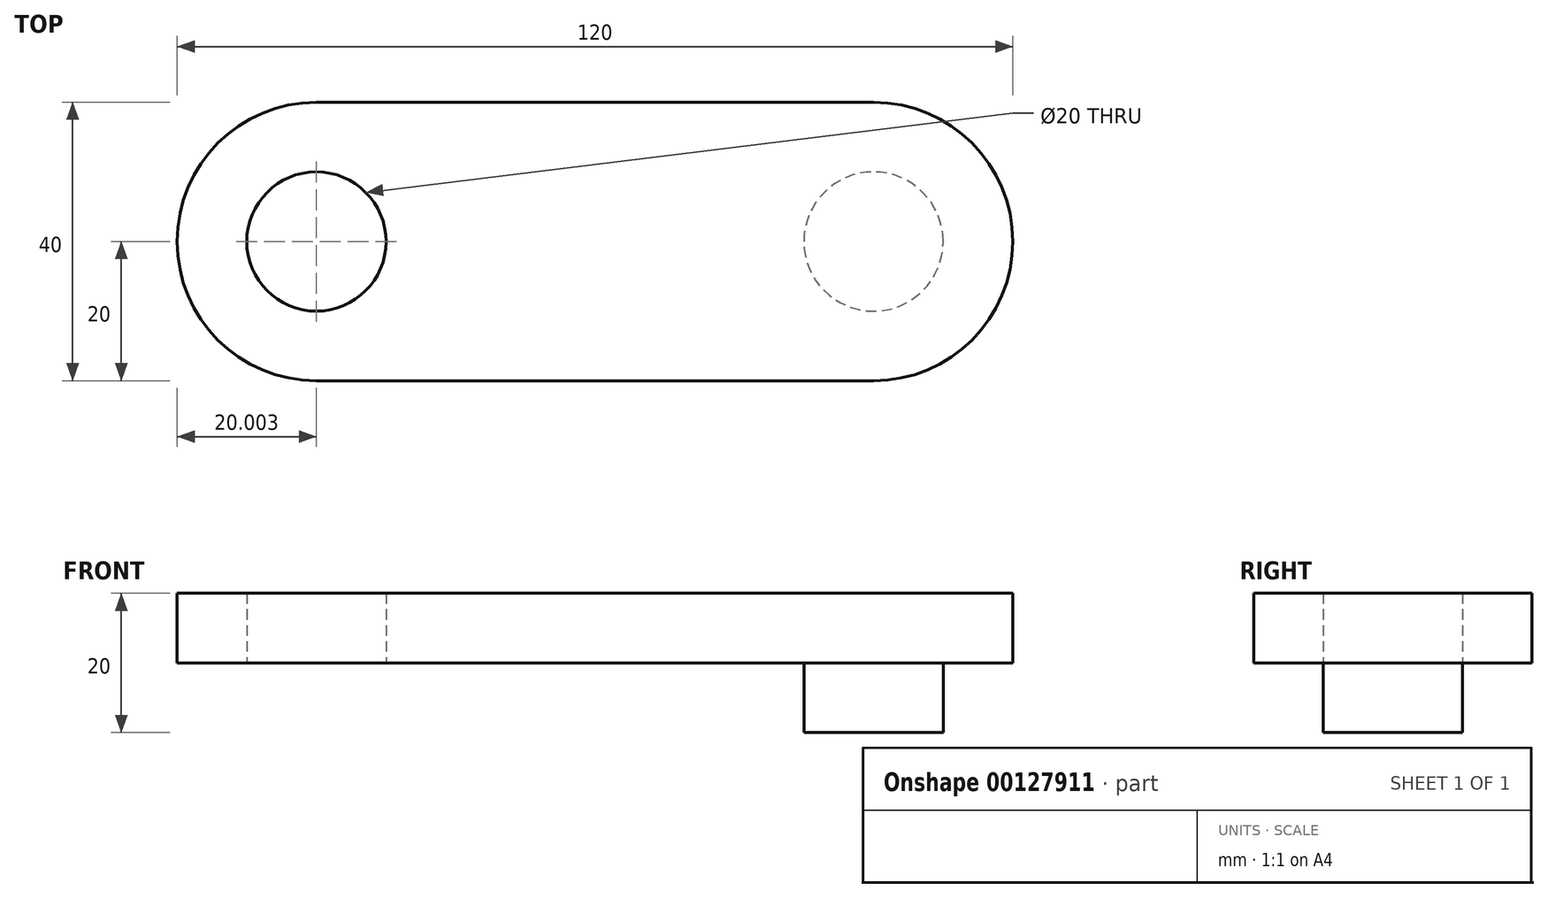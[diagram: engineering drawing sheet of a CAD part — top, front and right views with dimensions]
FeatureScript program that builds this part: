
annotation { "Feature Type Name" : "Feature", "Feature Type Description" : "" }
export const myFeature = defineFeature(function(context is Context, id is Id, definition is map)
    precondition{}
    {
        {
            var Q0;
            Q0=qCreatedBy(makeId("Top.planeOp"),FACE);
            var sketch = newSketch(context, id + "F0", { "sketchPlane" : qUnion([Q0])});
            skArc(sketch, "E0", {"start": v(-42.8, 20) * mm, "mid": v(-62.8, 0) * mm, "end": v(-42.8, -20) * mm});
            skLineSegment(sketch, "E1", {"start": v(-42.8, 20) * mm, "end": v(37.2, 20) * mm});
            skLineSegment(sketch, "E2", {"start": v(-42.8, -20) * mm, "end": v(37.2, -20) * mm});
            skArc(sketch, "E3", {"start": v(37.2, 20) * mm, "mid": v(57.2, 0) * mm, "end": v(37.2, -20) * mm});
            skCircle(sketch, "E4", {"center": v(-42.8, 0) * mm, "radius": 10 * mm});
            skSolve(sketch);
        }
        {
            var Q0;
            Q0 = qSketchRegion(id + "F0", true);
            extrude(context, id + "F1", {"entities" : qUnion([Q0]), "depth" : 10 * mm});
        }
        {
            var Q0;
            Q0=makeQuery(id+"F1.opExtrude","CAP_FACE",FACE,{"disambiguationData":[OSD([sQuery(id+"F0.wireOp",EDGE,"E0"),sQuery(id+"F0.wireOp",EDGE,"E1"),sQuery(id+"F0.wireOp",EDGE,"E2"),sQuery(id+"F0.wireOp",EDGE,"E3"),sQuery(id+"F0.wireOp",EDGE,"E4")])],"isStart":true});
            var sketch = newSketch(context, id + "F2", { "sketchPlane" : qUnion([Q0])});
            skCircle(sketch, "E5", {"center": v(37.2, 0) * mm, "radius": 10 * mm});
            skSolve(sketch);
        }
        {
            var Q0;
            Q0 = qSketchRegion(id + "F2", true);
            extrude(context, id + "F3", {"entities" : qUnion([Q0]), "operationType" : NewBodyOperationType.ADD, "depth" : 10 * mm});
        }
    });
